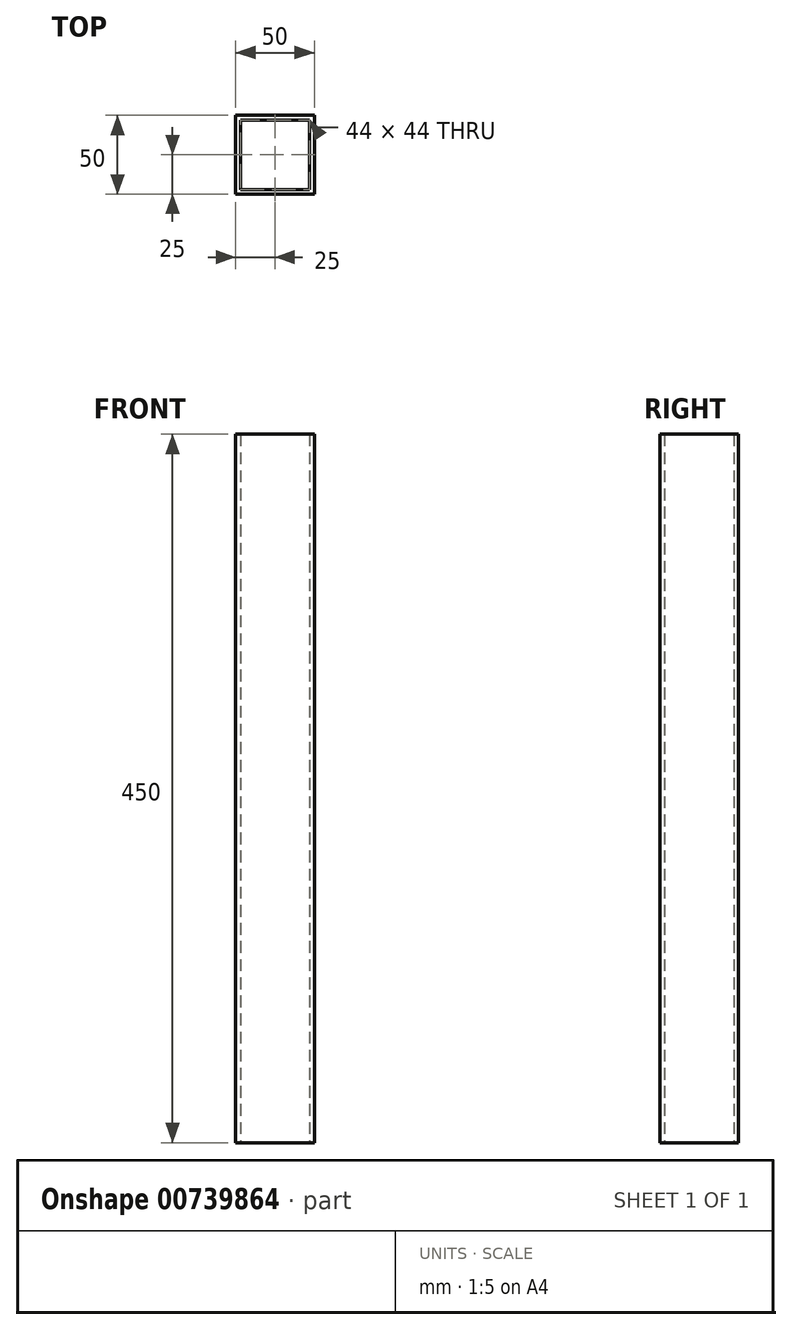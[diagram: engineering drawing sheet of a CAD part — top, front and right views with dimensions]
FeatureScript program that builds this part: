
annotation { "Feature Type Name" : "Feature", "Feature Type Description" : "" }
export const myFeature = defineFeature(function(context is Context, id is Id, definition is map)
    precondition{}
    {
        {
            var Q0;
            Q0=qCreatedBy(makeId("Top.planeOp"),FACE);
            var sketch = newSketch(context, id + "F0", { "sketchPlane" : qUnion([Q0])});
            skLineSegment(sketch, "E0.bottom", {"start": v(25, -25) * mm, "end": v(-25, -25) * mm});
            skLineSegment(sketch, "E0.top", {"start": v(25, 25) * mm, "end": v(-25, 25) * mm});
            skLineSegment(sketch, "E0.left", {"start": v(25, -25) * mm, "end": v(25, 25) * mm});
            skLineSegment(sketch, "E0.right", {"start": v(-25, -25) * mm, "end": v(-25, 25) * mm});
            skPoint(sketch, "E0.middle", {"position": v(0, 0) * mm});
            skLineSegment(sketch, "E1.0", {"start": v(-22, -22) * mm, "end": v(-22, 22) * mm});
            skLineSegment(sketch, "E1.1", {"start": v(22, -22) * mm, "end": v(-22, -22) * mm});
            skLineSegment(sketch, "E1.2", {"start": v(22, -22) * mm, "end": v(22, 22) * mm});
            skLineSegment(sketch, "E1.3", {"start": v(22, 22) * mm, "end": v(-22, 22) * mm});
            skSolve(sketch);
        }
        {
            var Q0;
            Q0 = qSketchRegion(id + "F0", true);
            extrude(context, id + "F1", {"entities" : qUnion([Q0]), "depth" : 450 * mm, "offsetDistance" : 25 * mm});
        }
    });
